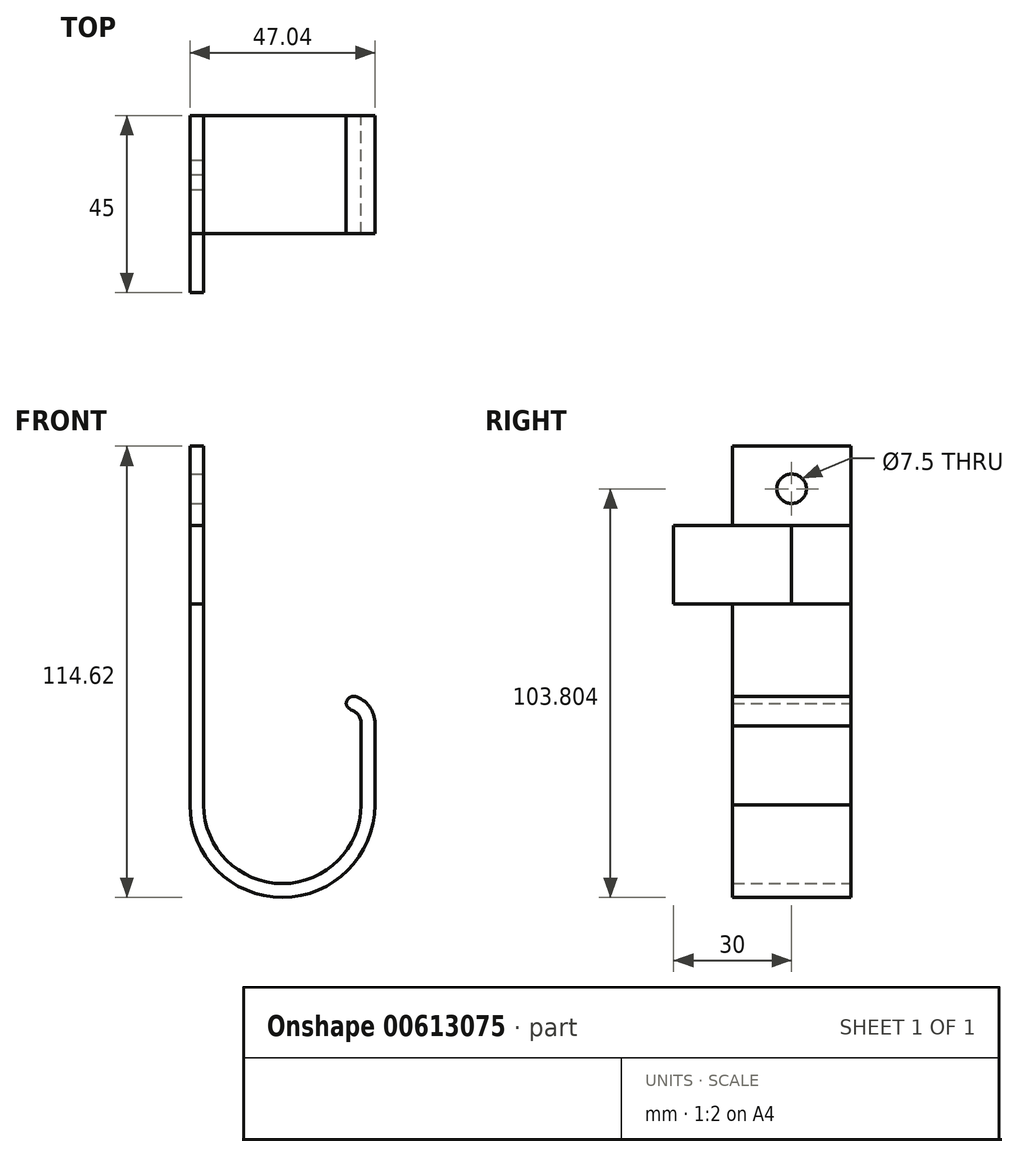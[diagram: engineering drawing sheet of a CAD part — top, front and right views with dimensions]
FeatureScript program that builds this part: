
annotation { "Feature Type Name" : "Feature", "Feature Type Description" : "" }
export const myFeature = defineFeature(function(context is Context, id is Id, definition is map)
    precondition{}
    {
        {
            var Q0;
            Q0=qCreatedBy(makeId("Front.planeOp"),FACE);
            var sketch = newSketch(context, id + "F0", { "sketchPlane" : qUnion([Q0])});
            skLineSegment(sketch, "E0.bottom", {"start": v(-24.15, 99.96) * mm, "end": v(-20.65, 99.96) * mm});
            skLineSegment(sketch, "E0.top", {"start": v(-24.15, 8.84) * mm, "end": v(-20.65, 8.84) * mm});
            skLineSegment(sketch, "E0.left", {"start": v(-24.15, 99.96) * mm, "end": v(-24.15, 8.84) * mm});
            skLineSegment(sketch, "E0.right", {"start": v(-20.65, 99.96) * mm, "end": v(-20.65, 8.84) * mm});
            skArc(sketch, "E1", {"start": v(-20.65, 8.84) * mm, "mid": v(-0.65, -11.16) * mm, "end": v(19.35, 8.84) * mm});
            skArc(sketch, "E2", {"start": v(-24.15, 8.84) * mm, "mid": v(-0.65, -14.66) * mm, "end": v(22.85, 8.84) * mm});
            skArc(sketch, "E3", {"start": v(-20.65, 65.98) * mm, "mid": v(-17.9, 82.97) * mm, "end": v(-20.65, 99.96) * mm});
            skLineSegment(sketch, "E4", {"start": v(-24.15, 29.96) * mm, "end": v(-20.65, 29.96) * mm});
            skLineSegment(sketch, "E5", {"start": v(19.35, 8.84) * mm, "end": v(22.85, 8.84) * mm});
            skLineSegment(sketch, "E6.bottom", {"start": v(19.21, 8.84) * mm, "end": v(19.35, 8.84) * mm});
            skLineSegment(sketch, "E7.bottom", {"start": v(19.35, 8.84) * mm, "end": v(22.87, 8.84) * mm});
            skLineSegment(sketch, "E7.top", {"start": v(19.35, 28.89) * mm, "end": v(22.87, 28.89) * mm});
            skLineSegment(sketch, "E7.left", {"start": v(19.35, 8.84) * mm, "end": v(19.35, 28.89) * mm});
            skLineSegment(sketch, "E7.right", {"start": v(22.87, 8.84) * mm, "end": v(22.87, 28.89) * mm});
            skLineSegment(sketch, "E8.bottom", {"start": v(-3.99, 36.8) * mm, "end": v(15.54, 36.8) * mm});
            skLineSegment(sketch, "E8.top", {"start": v(-3.99, 33.24) * mm, "end": v(15.54, 33.24) * mm});
            skLineSegment(sketch, "E8.left", {"start": v(-3.99, 36.8) * mm, "end": v(-3.99, 33.24) * mm});
            skLineSegment(sketch, "E8.right", {"start": v(15.54, 36.8) * mm, "end": v(15.54, 33.24) * mm});
            skArc(sketch, "E9", {"start": v(19.35, 28.89) * mm, "mid": v(18.43, 31.93) * mm, "end": v(15.54, 33.24) * mm});
            skArc(sketch, "E10", {"start": v(22.87, 28.89) * mm, "mid": v(20.94, 34.45) * mm, "end": v(15.54, 36.8) * mm});
            skLineSegment(sketch, "E11.bottom", {"start": v(-24.15, 79.85) * mm, "end": v(-20.65, 79.85) * mm});
            skLineSegment(sketch, "E11.top", {"start": v(-24.15, 59.82) * mm, "end": v(-20.65, 59.82) * mm});
            skLineSegment(sketch, "E11.left", {"start": v(-24.15, 79.85) * mm, "end": v(-24.15, 59.82) * mm});
            skLineSegment(sketch, "E11.right", {"start": v(-20.65, 79.85) * mm, "end": v(-20.65, 59.82) * mm});
            skSolve(sketch);
        }
        {
            var Q0;
            {var subQ2=sQuery(id+"F0.wireOp",EDGE,"E0.bottom");Q0=makeQuery(id+"F0.imprint","IMPRINT",FACE,{"disambiguationData":[TD([[makeQuery(id+"F0.imprint","IMPRINT",EDGE,{"derivedFrom":subQ2}),-1.0]])]});}
            var Q1;
            {var subQ0=sQuery(id+"F0.wireOp",EDGE,"E0.top");Q1=makeQuery(id+"F0.imprint","IMPRINT",FACE,{"disambiguationData":[TD([[makeQuery(id+"F0.imprint","IMPRINT",EDGE,{"derivedFrom":subQ0}),1.0]])]});}
            var Q2;
            Q2=makeQuery(id+"F0.imprint","IMPRINT",FACE,{"disambiguationData":[TD([[makeQuery(id+"F0.imprint","IMPRINT",EDGE,{"derivedFrom":sQuery(id+"F0.wireOp",EDGE,"E0.top")}),-1.0]])]});
            var Q3;
            Q3=makeQuery(id+"F0.imprint","IMPRINT",FACE,{"disambiguationData":[TD([[makeQuery(id+"F0.imprint","IMPRINT",EDGE,{"derivedFrom":sQuery(id+"F0.wireOp",EDGE,"E7.top")}),-1.0]])]});
            var Q4;
            Q4=makeQuery(id+"F0.imprint","IMPRINT",FACE,{"disambiguationData":[TD([[makeQuery(id+"F0.imprint","IMPRINT",EDGE,{"derivedFrom":sQuery(id+"F0.wireOp",EDGE,"E7.top")}),1.0]])]});
            var Q5;
            {var subQ0=sQuery(id+"F0.wireOp",EDGE,"E4");Q5=makeQuery(id+"F0.imprint","IMPRINT",FACE,{"disambiguationData":[TD([[makeQuery(id+"F0.imprint","IMPRINT",EDGE,{"derivedFrom":subQ0}),1.0]])]});}
            extrude(context, id + "F1", {"entities" : qUnion([Q0, Q1, Q2, Q3, Q4, Q5]), "endBound" : BoundingType.SYMMETRIC, "depth" : 30 * mm, "offsetDistance" : 25 * mm});
        }
        {
            var Q0;
            Q0=qCreatedBy(makeId("Right.planeOp"),FACE);
            var sketch = newSketch(context, id + "F2", { "sketchPlane" : qUnion([Q0])});
            skCircle(sketch, "E12", {"center": v(0, 89.14) * mm, "radius": 5 * mm});
            skSolve(sketch);
        }
        {
            var Q0;
            Q0=sQuery(id+"F2.wireOp",VERTEX,"E12.center");
            var Q1;
            Q1=makeQuery(id+"F1.opExtrude","SWEPT_BODY",BODY,{"disambiguationData":[OSD([sQuery(id+"F0.wireOp",EDGE,"E0.bottom"),sQuery(id+"F0.wireOp",EDGE,"E0.left"),sQuery(id+"F0.wireOp",EDGE,"E0.right"),sQuery(id+"F0.wireOp",EDGE,"E11.bottom")])]});
            hole(context, id + "F3", {"style" : HoleStyle.SIMPLE, "endStyle" : HoleEndStyle.THROUGH, "holeDiameter" : 7.5 * mm, "majorDiameter" : 5 * mm, "isTappedThrough" : true, "tappedDepth" : 12 * mm, "tapClearance" : 3, "locations" : qUnion([Q0]), "scope" : qUnion([Q1])});
        }
        {
            var Q0;
            Q0=makeQuery(id+"F1.opExtrude","SWEPT_EDGE",EDGE,{"disambiguationData":[OSD([sQuery(id+"F0.wireOp",EDGE,"E8.top"),sQuery(id+"F0.wireOp",EDGE,"E8.right"),sQuery(id+"F0.wireOp",EDGE,"E9")])]});
            var Q1;
            Q1=makeQuery(id+"F1.opExtrude","SWEPT_EDGE",EDGE,{"disambiguationData":[OSD([sQuery(id+"F0.wireOp",EDGE,"E8.bottom"),sQuery(id+"F0.wireOp",EDGE,"E8.right"),sQuery(id+"F0.wireOp",EDGE,"E10")])]});
            fillet(context, id + "F4", {"entities" : qUnion([Q0, Q1]), "radius" : 2 * mm, "tangentPropagation" : true, "allowEdgeOverflow" : false});
        }
        {
            var Q0;
            {var subQ2=sQuery(id+"F0.wireOp",EDGE,"E11.bottom");Q0=makeQuery(id+"F0.imprint","IMPRINT",FACE,{"disambiguationData":[TD([[makeQuery(id+"F0.imprint","IMPRINT",EDGE,{"derivedFrom":subQ2}),-1.0]])]});}
            extrude(context, id + "F5", {"entities" : qUnion([Q0]), "depth" : 30 * mm, "offsetDistance" : 25 * mm});
        }
        {
            var Q0;
            {var subQ2=sQuery(id+"F0.wireOp",EDGE,"E11.bottom");Q0=makeQuery(id+"F0.imprint","IMPRINT",FACE,{"disambiguationData":[TD([[makeQuery(id+"F0.imprint","IMPRINT",EDGE,{"derivedFrom":subQ2}),-1.0]])]});}
            extrude(context, id + "F6", {"entities" : qUnion([Q0]), "oppositeDirection" : true, "depth" : 15 * mm, "offsetDistance" : 25 * mm});
        }
    });
